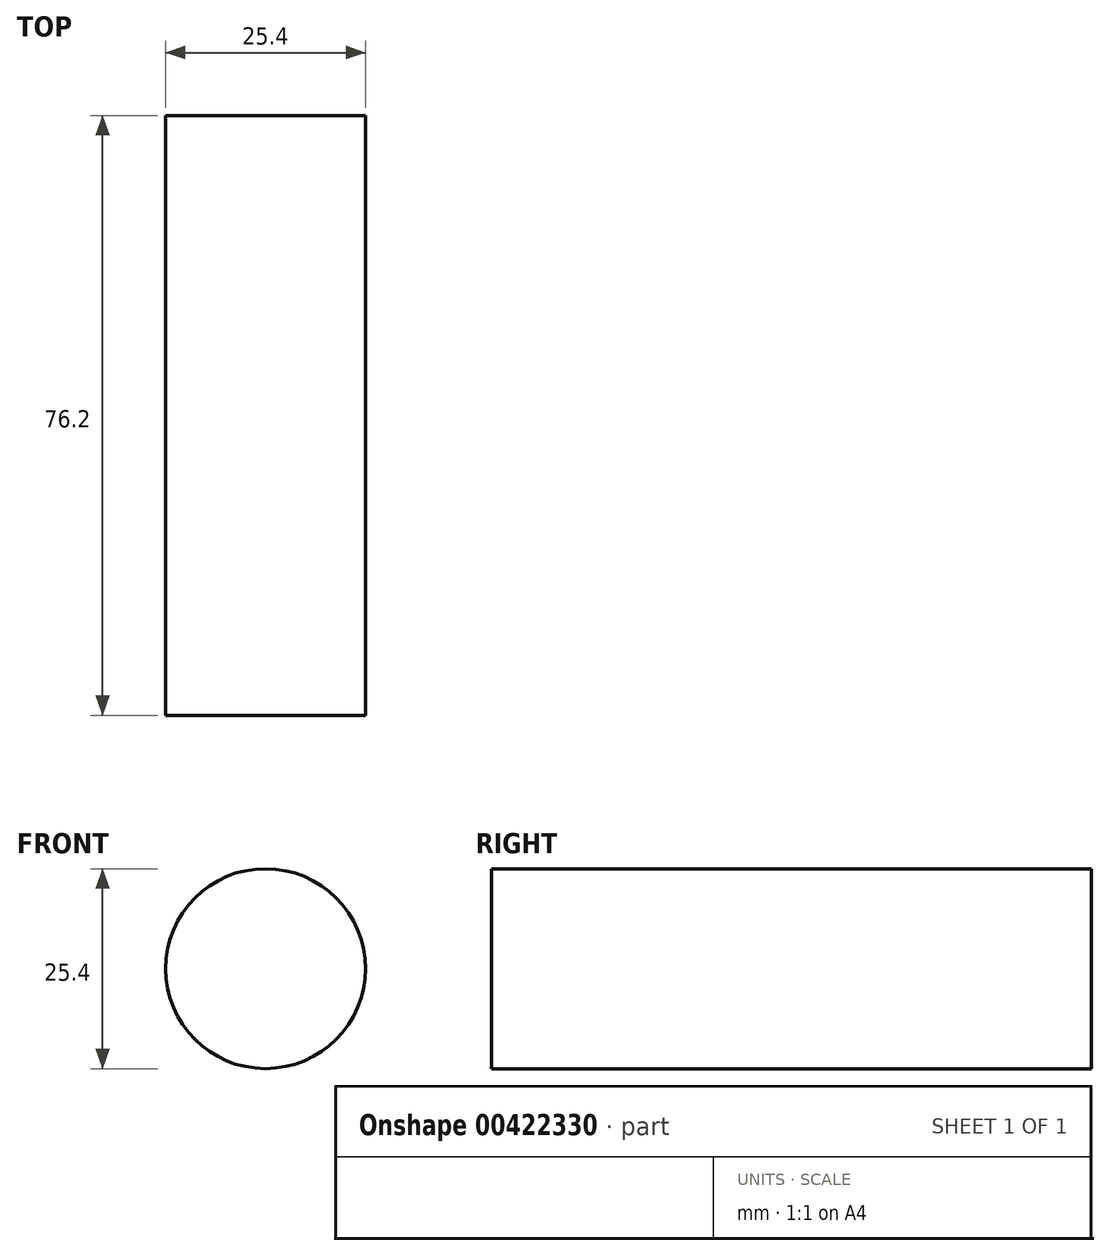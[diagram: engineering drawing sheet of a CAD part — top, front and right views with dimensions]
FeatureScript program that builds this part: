
annotation { "Feature Type Name" : "Feature", "Feature Type Description" : "" }
export const myFeature = defineFeature(function(context is Context, id is Id, definition is map)
    precondition{}
    {
        {
            var Q0;
            Q0=qCreatedBy(makeId("Front.planeOp"),FACE);
            var sketch = newSketch(context, id + "F0", { "sketchPlane" : qUnion([Q0])});
            skCircle(sketch, "E0", {"center": v(-15, 15.55) * mm, "radius": 12.7 * mm});
            skSolve(sketch);
        }
        {
            var Q0;
            Q0 = qSketchRegion(id + "F0", true);
            extrude(context, id + "F1", {"entities" : qUnion([Q0]), "depth" : 76.2 * mm});
        }
    });
